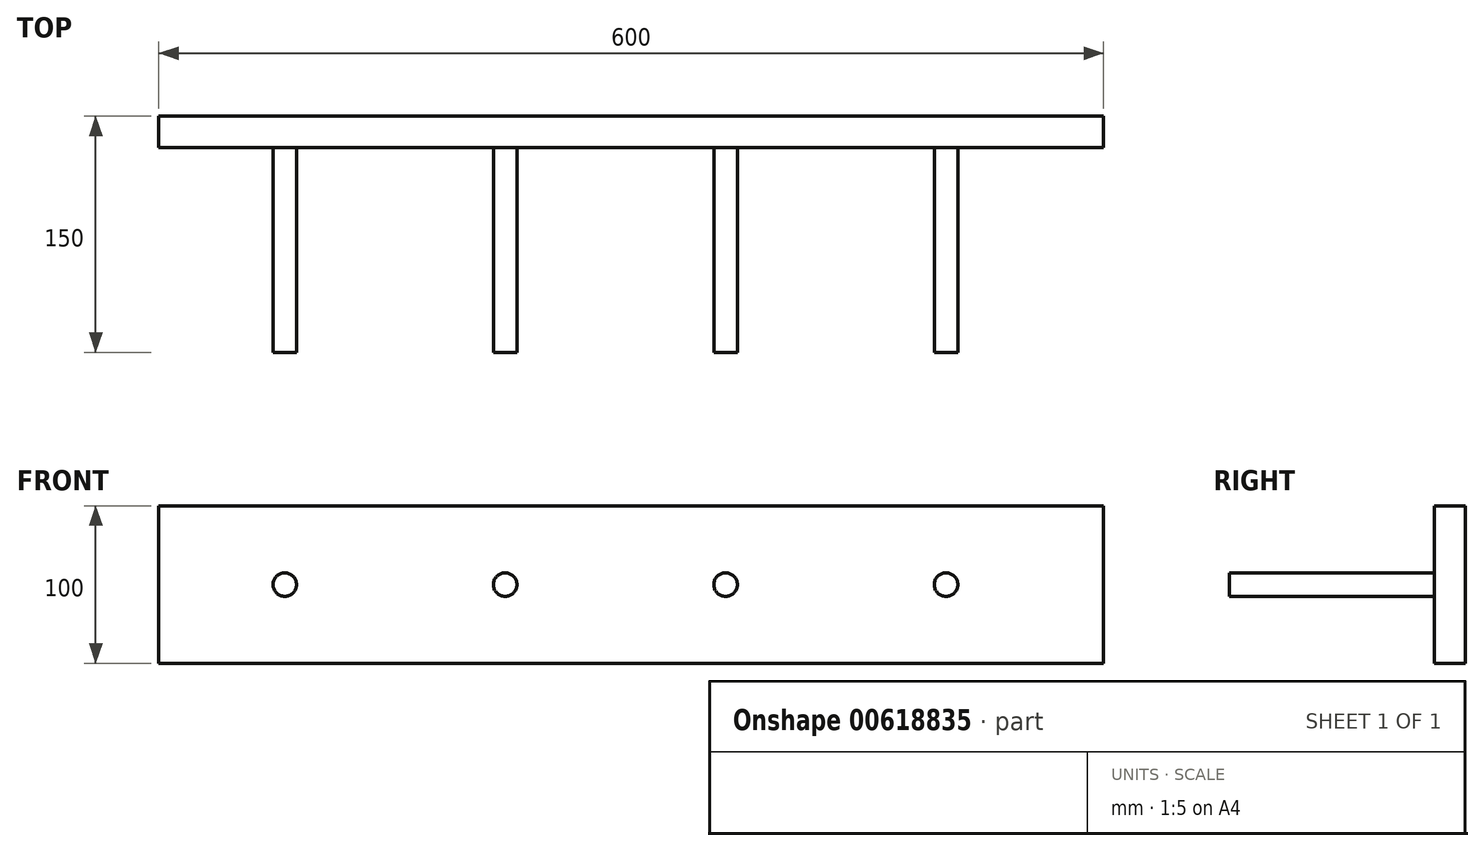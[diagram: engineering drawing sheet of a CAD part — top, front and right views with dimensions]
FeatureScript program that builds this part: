
annotation { "Feature Type Name" : "Feature", "Feature Type Description" : "" }
export const myFeature = defineFeature(function(context is Context, id is Id, definition is map)
    precondition{}
    {
        {
            var Q0;
            Q0=qCreatedBy(makeId("Front.planeOp"),FACE);
            var sketch = newSketch(context, id + "F0", { "sketchPlane" : qUnion([Q0])});
            skLineSegment(sketch, "E0.bottom", {"start": v(-300, 50) * mm, "end": v(300, 50) * mm});
            skLineSegment(sketch, "E0.top", {"start": v(-300, -50) * mm, "end": v(300, -50) * mm});
            skLineSegment(sketch, "E0.left", {"start": v(-300, 50) * mm, "end": v(-300, -50) * mm});
            skLineSegment(sketch, "E0.right", {"start": v(300, 50) * mm, "end": v(300, -50) * mm});
            skPoint(sketch, "E0.middle", {"position": v(0, 0) * mm});
            skSolve(sketch);
        }
        {
            var Q0;
            Q0 = qSketchRegion(id + "F0", true);
            extrude(context, id + "F1", {"entities" : qUnion([Q0]), "depth" : 20 * mm, "offsetDistance" : 25 * mm});
        }
        {
            var Q0;
            Q0=makeQuery(id+"F1.opExtrude","CAP_FACE",FACE,{"disambiguationData":[OSD([sQuery(id+"F0.wireOp",EDGE,"E0.bottom"),sQuery(id+"F0.wireOp",EDGE,"E0.top"),sQuery(id+"F0.wireOp",EDGE,"E0.left"),sQuery(id+"F0.wireOp",EDGE,"E0.right")])],"isStart":false});
            var sketch = newSketch(context, id + "F2", { "sketchPlane" : qUnion([Q0])});
            skCircle(sketch, "E1", {"center": v(-220, 0) * mm, "radius": 7.5 * mm});
            skCircle(sketch, "E2", {"center": v(-80, 0) * mm, "radius": 7.5 * mm});
            skCircle(sketch, "E3", {"center": v(60, 0) * mm, "radius": 7.5 * mm});
            skCircle(sketch, "E4", {"center": v(200, 0) * mm, "radius": 7.5 * mm});
            skSolve(sketch);
        }
        {
            var Q0;
            Q0 = qSketchRegion(id + "F2", true);
            extrude(context, id + "F3", {"entities" : qUnion([Q0]), "operationType" : NewBodyOperationType.ADD, "depth" : 130 * mm, "offsetDistance" : 25 * mm});
        }
    });
